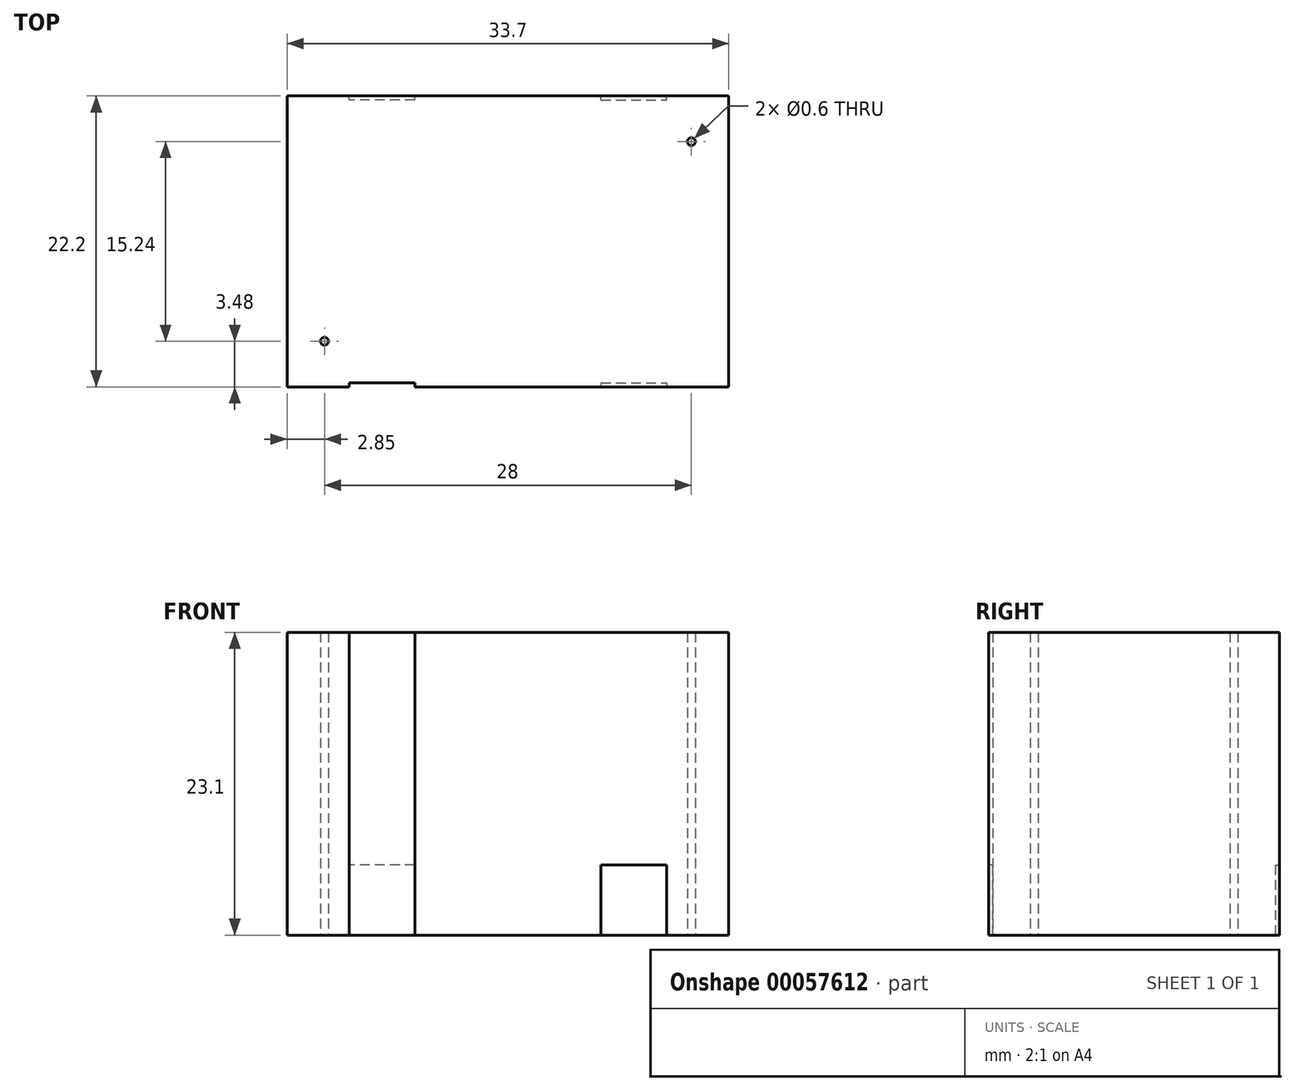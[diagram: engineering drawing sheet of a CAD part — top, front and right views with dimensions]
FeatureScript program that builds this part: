
annotation { "Feature Type Name" : "Feature", "Feature Type Description" : "" }
export const myFeature = defineFeature(function(context is Context, id is Id, definition is map)
    precondition{}
    {
        {
            var Q0;
            Q0=qCreatedBy(makeId("Top.planeOp"),FACE);
            var sketch = newSketch(context, id + "F0", { "sketchPlane" : qUnion([Q0])});
            skLineSegment(sketch, "E0.rect.bottom", {"start": v(16.85, -11.1) * mm, "end": v(-16.85, -11.1) * mm});
            skLineSegment(sketch, "E0.rect.top", {"start": v(16.85, 11.1) * mm, "end": v(-16.85, 11.1) * mm});
            skLineSegment(sketch, "E0.rect.left", {"start": v(16.85, -11.1) * mm, "end": v(16.85, 11.1) * mm});
            skLineSegment(sketch, "E0.rect.right", {"start": v(-16.85, -11.1) * mm, "end": v(-16.85, 11.1) * mm});
            skPoint(sketch, "E0.rect.middle", {"position": v(0, 0) * mm});
            skLineSegment(sketch, "E1", {"start": v(-20.18, 0) * mm, "end": v(19.5, 0) * mm, "construction": true});
            skLineSegment(sketch, "E2", {"start": v(0, -12.87) * mm, "end": v(0, 12.54) * mm, "construction": true});
            skPoint(sketch, "E2.endSnap0", {"position": v(0, 11.1) * mm});
            skCircle(sketch, "E3", {"center": v(-14, 7.62) * mm, "radius": 0.3 * mm});
            skCircle(sketch, "E4", {"center": v(14, 0) * mm, "radius": 0.3 * mm});
            skCircle(sketch, "E5.MirrorC", {"center": v(-14, -7.62) * mm, "radius": 0.3 * mm});
            skLineSegment(sketch, "E6.rect.bottom", {"start": v(-7.1, 10.8) * mm, "end": v(-12.1, 10.8) * mm});
            skLineSegment(sketch, "E6.rect.top", {"start": v(-7.1, 11.1) * mm, "end": v(-12.1, 11.1) * mm});
            skLineSegment(sketch, "E6.rect.left", {"start": v(-7.1, 10.8) * mm, "end": v(-7.1, 11.1) * mm});
            skLineSegment(sketch, "E6.rect.right", {"start": v(-12.1, 10.8) * mm, "end": v(-12.1, 11.1) * mm});
            skPoint(sketch, "E6.rect.middle", {"position": v(-9.6, 10.95) * mm});
            skLineSegment(sketch, "E7.MirrorCS", {"start": v(7.1, 10.8) * mm, "end": v(12.1, 10.8) * mm});
            skLineSegment(sketch, "E8.MirrorCS", {"start": v(12.1, 10.8) * mm, "end": v(12.1, 11.1) * mm});
            skLineSegment(sketch, "E9.MirrorCS", {"start": v(7.1, 10.8) * mm, "end": v(7.1, 11.1) * mm});
            skLineSegment(sketch, "E10.MirrorCS", {"start": v(7.1, 11.1) * mm, "end": v(12.1, 11.1) * mm});
            skLineSegment(sketch, "E11.MirrorCS", {"start": v(-7.1, -11.1) * mm, "end": v(-12.1, -11.1) * mm});
            skLineSegment(sketch, "E12.MirrorCS", {"start": v(-7.1, -10.8) * mm, "end": v(-12.1, -10.8) * mm});
            skLineSegment(sketch, "E13.MirrorCS", {"start": v(-12.1, -10.8) * mm, "end": v(-12.1, -11.1) * mm});
            skLineSegment(sketch, "E14.MirrorCS", {"start": v(-7.1, -10.8) * mm, "end": v(-7.1, -11.1) * mm});
            skLineSegment(sketch, "E15.MirrorCS", {"start": v(7.1, -10.8) * mm, "end": v(12.1, -10.8) * mm});
            skLineSegment(sketch, "E16.MirrorCS", {"start": v(7.1, -10.8) * mm, "end": v(7.1, -11.1) * mm});
            skLineSegment(sketch, "E17.MirrorCS", {"start": v(12.1, -10.8) * mm, "end": v(12.1, -11.1) * mm});
            skLineSegment(sketch, "E18.MirrorCS", {"start": v(7.1, -11.1) * mm, "end": v(12.1, -11.1) * mm});
            skCircle(sketch, "E19.MirrorC", {"center": v(14, 7.62) * mm, "radius": 0.3 * mm});
            skSolve(sketch);
        }
        {
            var Q0;
            {var subQ5=sQuery(id+"F0.wireOp",EDGE,"E0.rect.left");Q0=makeQuery(id+"F0.imprint","IMPRINT",FACE,{"disambiguationData":[TD([[makeQuery(id+"F0.imprint","IMPRINT",EDGE,{"derivedFrom":subQ5}),1.0]])]});}
            var Q1;
            Q1=makeQuery(id+"F0.imprint","IMPRINT",FACE,{"disambiguationData":[TD([[makeQuery(id+"F0.imprint","IMPRINT",EDGE,{"derivedFrom":sQuery(id+"F0.wireOp",EDGE,"E6.rect.bottom")}),-1.0]])]});
            var Q2;
            Q2=makeQuery(id+"F0.imprint","IMPRINT",FACE,{"disambiguationData":[TD([[makeQuery(id+"F0.imprint","IMPRINT",EDGE,{"derivedFrom":sQuery(id+"F0.wireOp",EDGE,"E7.MirrorCS")}),1.0]])]});
            var Q3;
            Q3=makeQuery(id+"F0.imprint","IMPRINT",FACE,{"disambiguationData":[TD([[makeQuery(id+"F0.imprint","IMPRINT",EDGE,{"derivedFrom":sQuery(id+"F0.wireOp",EDGE,"E15.MirrorCS")}),-1.0]])]});
            var Q4;
            Q4=makeQuery(id+"F0.imprint","IMPRINT",FACE,{"disambiguationData":[TD([[makeQuery(id+"F0.imprint","IMPRINT",EDGE,{"derivedFrom":sQuery(id+"F0.wireOp",EDGE,"E11.MirrorCS")}),-1.0]])]});
            var Q5;
            Q5=makeQuery(id+"F0.imprint","IMPRINT",FACE,{"disambiguationData":[TD([[makeQuery(id+"F0.imprint","IMPRINT",EDGE,{"derivedFrom":sQuery(id+"F0.wireOp",EDGE,"E5.MirrorC")}),-1.0]])]});
            var Q6;
            Q6=makeQuery(id+"F0.imprint","IMPRINT",FACE,{"disambiguationData":[TD([[makeQuery(id+"F0.imprint","IMPRINT",EDGE,{"derivedFrom":sQuery(id+"F0.wireOp",EDGE,"E3")}),1.0]])]});
            var Q7;
            Q7=makeQuery(id+"F0.imprint","IMPRINT",FACE,{"disambiguationData":[TD([[makeQuery(id+"F0.imprint","IMPRINT",EDGE,{"derivedFrom":sQuery(id+"F0.wireOp",EDGE,"00325824-9c94-421b-ac06-6b14c01ca1070.MirrorC")}),1.0]])]});
            var Q8;
            Q8=makeQuery(id+"F0.imprint","IMPRINT",FACE,{"disambiguationData":[TD([[makeQuery(id+"F0.imprint","IMPRINT",EDGE,{"derivedFrom":sQuery(id+"F0.wireOp",EDGE,"E4")}),1.0]])]});
            var Q9;
            Q9=makeQuery(id+"F0.imprint","IMPRINT",FACE,{"disambiguationData":[TD([[makeQuery(id+"F0.imprint","IMPRINT",EDGE,{"derivedFrom":sQuery(id+"F0.wireOp",EDGE,"E19.MirrorC")}),-1.0]])]});
            extrude(context, id + "F1", {"entities" : qUnion([Q0, Q1, Q2, Q3, Q4, Q5, Q6, Q7, Q8, Q9]), "depth" : 17 * mm});
        }
        {
            var Q0;
            Q0=makeQuery(id+"F0.imprint","IMPRINT",FACE,{"disambiguationData":[TD([[makeQuery(id+"F0.imprint","IMPRINT",EDGE,{"derivedFrom":sQuery(id+"F0.wireOp",EDGE,"E7.MirrorCS")}),1.0]])]});
            var Q1;
            Q1=makeQuery(id+"F0.imprint","IMPRINT",FACE,{"disambiguationData":[TD([[makeQuery(id+"F0.imprint","IMPRINT",EDGE,{"derivedFrom":sQuery(id+"F0.wireOp",EDGE,"E6.rect.bottom")}),-1.0]])]});
            var Q2;
            Q2=makeQuery(id+"F0.imprint","IMPRINT",FACE,{"disambiguationData":[TD([[makeQuery(id+"F0.imprint","IMPRINT",EDGE,{"derivedFrom":sQuery(id+"F0.wireOp",EDGE,"E11.MirrorCS")}),-1.0]])]});
            var Q3;
            Q3=makeQuery(id+"F0.imprint","IMPRINT",FACE,{"disambiguationData":[TD([[makeQuery(id+"F0.imprint","IMPRINT",EDGE,{"derivedFrom":sQuery(id+"F0.wireOp",EDGE,"E15.MirrorCS")}),-1.0]])]});
            extrude(context, id + "F2", {"entities" : qUnion([Q0, Q1, Q2, Q3]), "operationType" : NewBodyOperationType.ADD, "oppositeDirection" : true, "depth" : .75 * mm});
        }
        {
            var Q0;
            Q0=makeQuery(id+"F0.imprint","IMPRINT",FACE,{"disambiguationData":[TD([[makeQuery(id+"F0.imprint","IMPRINT",EDGE,{"derivedFrom":sQuery(id+"F0.wireOp",EDGE,"00325824-9c94-421b-ac06-6b14c01ca1070.MirrorC")}),1.0]])]});
            var Q1;
            Q1=makeQuery(id+"F0.imprint","IMPRINT",FACE,{"disambiguationData":[TD([[makeQuery(id+"F0.imprint","IMPRINT",EDGE,{"derivedFrom":sQuery(id+"F0.wireOp",EDGE,"E4")}),1.0]])]});
            var Q2;
            Q2=makeQuery(id+"F0.imprint","IMPRINT",FACE,{"disambiguationData":[TD([[makeQuery(id+"F0.imprint","IMPRINT",EDGE,{"derivedFrom":sQuery(id+"F0.wireOp",EDGE,"E3")}),1.0]])]});
            var Q3;
            Q3=makeQuery(id+"F0.imprint","IMPRINT",FACE,{"disambiguationData":[TD([[makeQuery(id+"F0.imprint","IMPRINT",EDGE,{"derivedFrom":sQuery(id+"F0.wireOp",EDGE,"E5.MirrorC")}),-1.0]])]});
            var Q4;
            Q4=makeQuery(id+"F0.imprint","IMPRINT",FACE,{"disambiguationData":[TD([[makeQuery(id+"F0.imprint","IMPRINT",EDGE,{"derivedFrom":sQuery(id+"F0.wireOp",EDGE,"E19.MirrorC")}),-1.0]])]});
            var Q5;
            Q5=sQuery(id+"F0.wireOp",EDGE,"E4");
            var Q6;
            Q6=sQuery(id+"F0.wireOp",EDGE,"00325824-9c94-421b-ac06-6b14c01ca1070.MirrorC");
            var Q7;
            Q7=sQuery(id+"F0.wireOp",EDGE,"E3");
            var Q8;
            Q8=sQuery(id+"F0.wireOp",EDGE,"E5.MirrorC");
            extrude(context, id + "F3", {"entities" : qUnion([Q0, Q1, Q2, Q3, Q4]), "operationType" : NewBodyOperationType.ADD, "surfaceEntities" : qUnion([Q5, Q6, Q7, Q8]), "oppositeDirection" : true, "depth" : 6.1 * mm});
        }
    });
